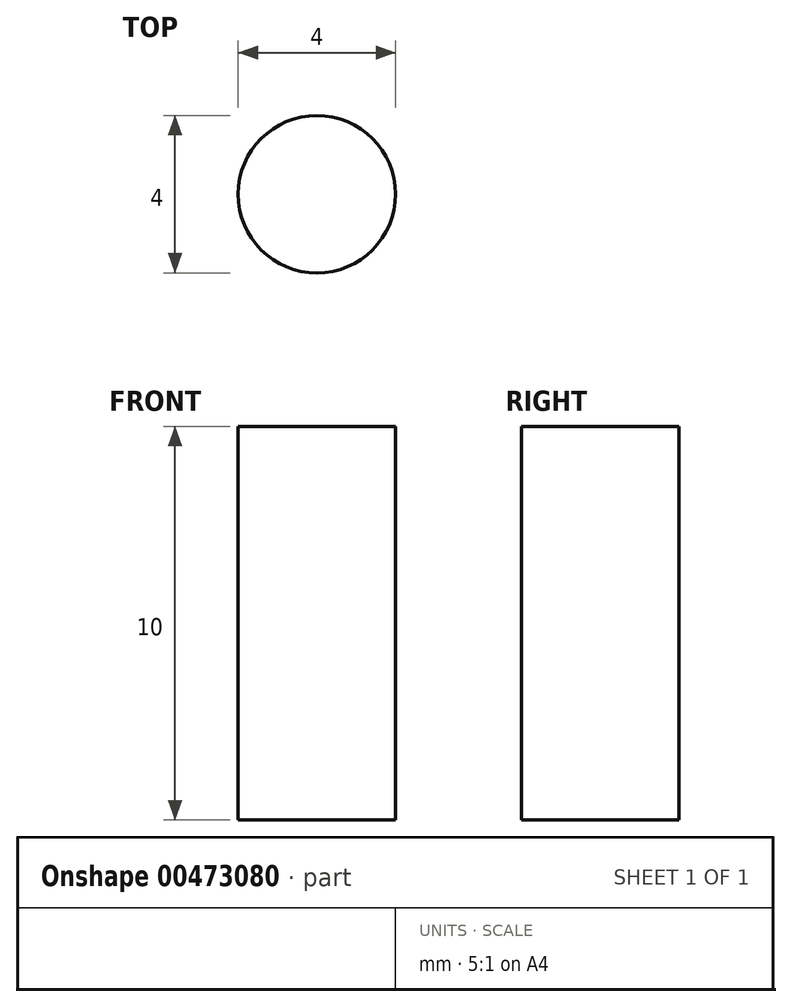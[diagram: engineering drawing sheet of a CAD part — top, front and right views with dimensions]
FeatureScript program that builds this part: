
annotation { "Feature Type Name" : "Feature", "Feature Type Description" : "" }
export const myFeature = defineFeature(function(context is Context, id is Id, definition is map)
    precondition{}
    {
        {
            var Q0;
            Q0=qCreatedBy(makeId("Top.planeOp"),FACE);
            var sketch = newSketch(context, id + "F0", { "sketchPlane" : qUnion([Q0])});
            skCircle(sketch, "E0", {"center": v(0, 0) * mm, "radius": 2 * mm});
            skSolve(sketch);
        }
        {
            var Q0;
            Q0=qSketchRegion(id+"F0",true);
            extrude(context, id + "F1", {"entities" : qUnion([Q0]), "depth" : 10 * mm});
        }
    });
